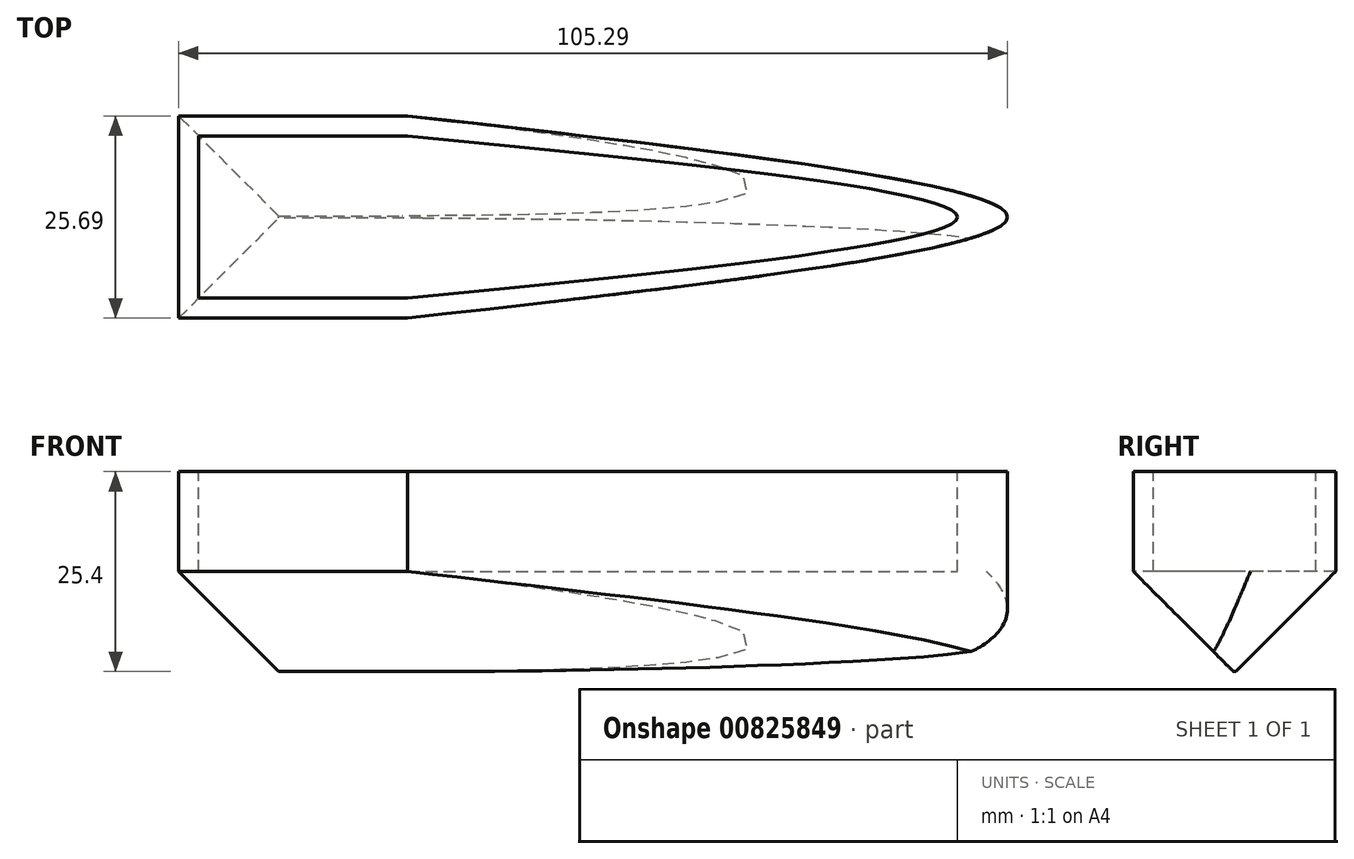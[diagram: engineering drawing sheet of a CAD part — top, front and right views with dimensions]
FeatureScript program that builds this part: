
annotation { "Feature Type Name" : "Feature", "Feature Type Description" : "" }
export const myFeature = defineFeature(function(context is Context, id is Id, definition is map)
    precondition{}
    {
        {
            var Q0;
            Q0=qCreatedBy(makeId("Top.planeOp"),FACE);
            var sketch = newSketch(context, id + "F0", { "sketchPlane" : qUnion([Q0])});
            skLineSegment(sketch, "E0.bottom", {"start": v(-35.39, 17.34) * mm, "end": v(-64.48, 17.34) * mm});
            skLineSegment(sketch, "E0.top", {"start": v(-35.39, -8.35) * mm, "end": v(-64.48, -8.35) * mm});
            skLineSegment(sketch, "E0.left", {"start": v(-35.39, 17.34) * mm, "end": v(-35.39, -8.35) * mm});
            skLineSegment(sketch, "E0.right", {"start": v(-64.48, 17.34) * mm, "end": v(-64.48, -8.35) * mm});
            skLineSegment(sketch, "E1", {"start": v(-35.39, 4.5) * mm, "end": v(40.81, 4.5) * mm});
            skFitSpline(sketch, "E2", {"points": [v(-35.39, -8.35) * mm, v(40.81, 4.5) * mm, v(-35.39, 17.34) * mm], "startDerivative": vector(228.6, 25.7) * mm, "endDerivative": vector(-228.6, 25.7) * mm});
            skSolve(sketch);
        }
        {
            var Q0;
            Q0 = qSketchRegion(id + "F0", true);
            extrude(context, id + "F1", {"entities" : qUnion([Q0]), "depth" : 25.4 * mm, "offsetDistance" : 25.4 * mm});
        }
        {
            var Q0;
            Q0=makeQuery(id+"F1.opExtrude","CAP_EDGE",EDGE,{"disambiguationData":[OSD([sQuery(id+"F0.wireOp",EDGE,"E0.bottom")])],"isStart":true});
            var Q1;
            Q1=makeQuery(id+"F1.opExtrude","CAP_EDGE",EDGE,{"disambiguationData":[OSD([sQuery(id+"F0.wireOp",EDGE,"E0.top")])],"isStart":true});
            var Q2;
            Q2=makeQuery(id+"F1.opExtrude","CAP_EDGE",EDGE,{"disambiguationData":[OSD([sQuery(id+"F0.wireOp",EDGE,"E0.right")])],"isStart":true});
            chamfer(context, id + "F2", {"entities" : qUnion([Q0, Q1, Q2]), "width" : 12.7 * mm, "tangentPropagation" : true});
        }
        {
            var Q0;
            Q0=makeQuery(id+"F1.opExtrude","CAP_EDGE",EDGE,{"disambiguationData":[OSD([sQuery(id+"F0.wireOp",EDGE,"E2")])],"isStart":true});
            fillet(context, id + "F3", {"entities" : qUnion([Q0]), "radius" : 12.7 * mm, "tangentPropagation" : true, "allowEdgeOverflow" : false});
        }
        {
            var Q0;
            Q0=makeQuery(id+"F1.opExtrude","CAP_FACE",FACE,{"disambiguationData":[OSD([sQuery(id+"F0.wireOp",EDGE,"E0.bottom"),sQuery(id+"F0.wireOp",EDGE,"E0.top"),sQuery(id+"F0.wireOp",EDGE,"E0.right"),sQuery(id+"F0.wireOp",EDGE,"E2")])],"isStart":false});
            var sketch = newSketch(context, id + "F4", { "sketchPlane" : qUnion([Q0])});
            skLineSegment(sketch, "E3.bottom", {"start": v(-61.94, 14.8) * mm, "end": v(-35.39, 14.8) * mm});
            skLineSegment(sketch, "E3.top", {"start": v(-61.94, -5.8) * mm, "end": v(-35.39, -5.8) * mm});
            skLineSegment(sketch, "E3.left", {"start": v(-61.94, 14.8) * mm, "end": v(-61.94, -5.8) * mm});
            skLineSegment(sketch, "E3.right", {"start": v(-35.39, 14.8) * mm, "end": v(-35.39, -5.8) * mm});
            skLineSegment(sketch, "E4", {"start": v(-35.39, 4.5) * mm, "end": v(34.46, 4.5) * mm});
            skFitSpline(sketch, "E5", {"points": [v(-35.39, 14.8) * mm, v(34.46, 4.5) * mm, v(-35.39, -5.8) * mm], "startDerivative": vector(209.55, -20.61) * mm, "endDerivative": vector(-209.55, -20.61) * mm});
            skSolve(sketch);
        }
        {
            var Q0;
            {var subQ3=sQuery(id+"F4.wireOp",EDGE,"E4");Q0=makeQuery(id+"F4.imprint","IMPRINT",FACE,{"disambiguationData":[TD([[makeQuery(id+"F4.imprint","IMPRINT",EDGE,{"derivedFrom":subQ3}),1.0]])]});}
            var Q1;
            {var subQ3=sQuery(id+"F4.wireOp",EDGE,"E4");Q1=makeQuery(id+"F4.imprint","IMPRINT",FACE,{"disambiguationData":[TD([[makeQuery(id+"F4.imprint","IMPRINT",EDGE,{"derivedFrom":subQ3}),-1.0]])]});}
            var Q2;
            {var subQ2=sQuery(id+"F4.wireOp",EDGE,"E3.bottom");Q2=makeQuery(id+"F4.imprint","IMPRINT",FACE,{"disambiguationData":[TD([[makeQuery(id+"F4.imprint","IMPRINT",EDGE,{"derivedFrom":subQ2}),-1.0]])]});}
            extrude(context, id + "F5", {"entities" : qUnion([Q0, Q1, Q2]), "operationType" : NewBodyOperationType.REMOVE, "oppositeDirection" : true, "depth" : 12.7 * mm, "offsetDistance" : 25.4 * mm});
        }
    });
